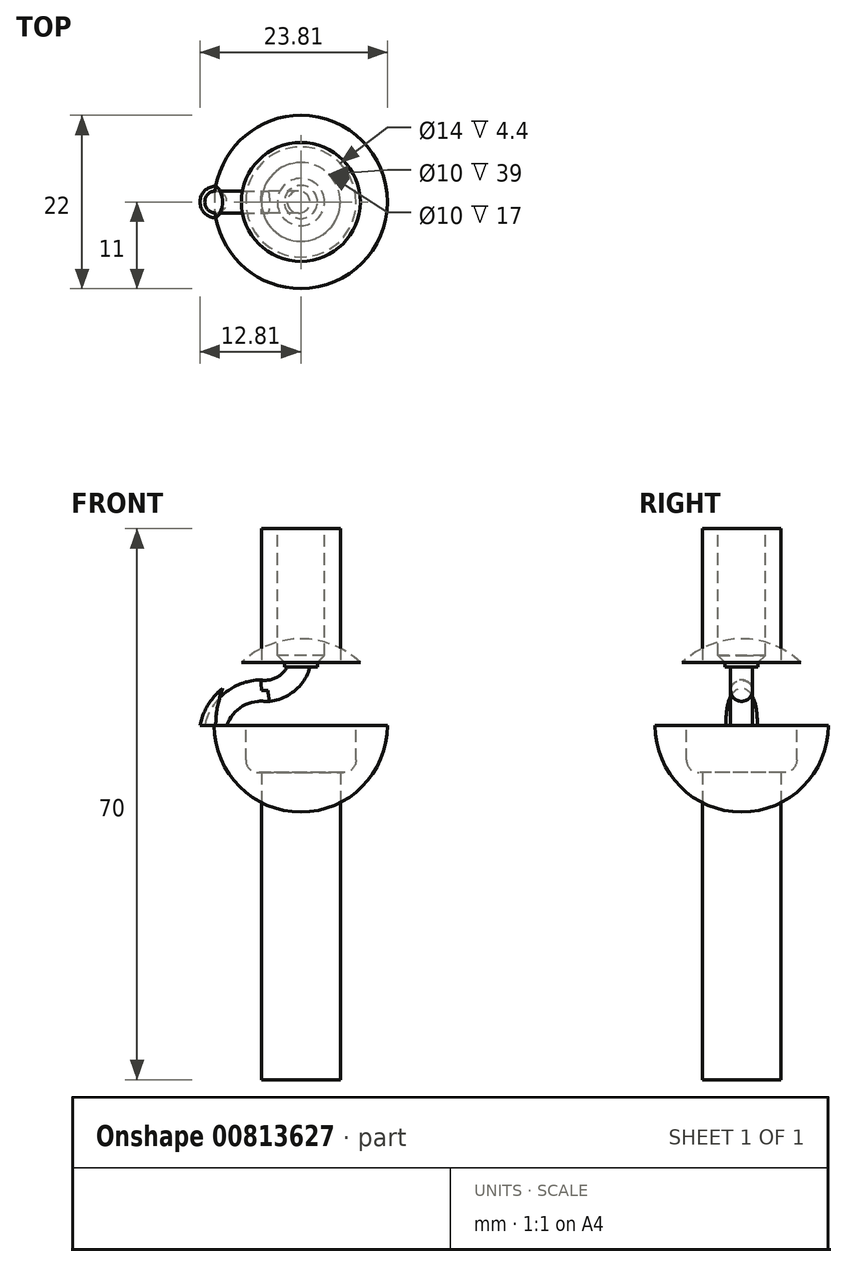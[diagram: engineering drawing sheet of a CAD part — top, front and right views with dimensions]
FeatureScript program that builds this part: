
annotation { "Feature Type Name" : "Feature", "Feature Type Description" : "" }
export const myFeature = defineFeature(function(context is Context, id is Id, definition is map)
    precondition{}
    {
        {
            var Q0;
            Q0=qCreatedBy(makeId("Top.planeOp"),FACE);
            var sketch = newSketch(context, id + "F0", { "sketchPlane" : qUnion([Q0])});
            skArc(sketch, "E0", {"start": v(6, 0) * mm, "mid": v(0, 6) * mm, "end": v(-6, 0) * mm});
            skLineSegment(sketch, "E1", {"start": v(-6, 0) * mm, "end": v(6, 0) * mm});
            skSolve(sketch);
        }
        {
            var Q0;
            Q0=makeQuery(id+"F0.imprint","IMPRINT",FACE,{"disambiguationData":[TD([[makeQuery(id+"F0.imprint","IMPRINT",EDGE,{"derivedFrom":sQuery(id+"F0.wireOp",EDGE,"E0")}),1.0]])]});
            var Q1;
            Q1=sQuery(id+"F0.wireOp",EDGE,"E1");
            revolve(context, id + "F1", {"surfaceOperationType" : NewSurfaceOperationType.NEW, "entities" : qUnion([Q0]), "axis" : qUnion([Q1]), "revolveType" : RevolveType.ONE_DIRECTION, "angle" : 180 * degree});
        }
        {
            var Q0;
            Q0=qCreatedBy(makeId("Front.planeOp"),FACE);
            var sketch = newSketch(context, id + "F2", { "sketchPlane" : qUnion([Q0])});
            skLineSegment(sketch, "E2.bottom", {"start": v(-10.2, 6.03) * mm, "end": v(11.74, 6.03) * mm});
            skLineSegment(sketch, "E2.top", {"start": v(-10.2, 4) * mm, "end": v(11.74, 4) * mm});
            skLineSegment(sketch, "E2.left", {"start": v(-10.2, 6.03) * mm, "end": v(-10.2, 4) * mm});
            skLineSegment(sketch, "E2.right", {"start": v(11.74, 6.03) * mm, "end": v(11.74, 4) * mm});
            skSolve(sketch);
        }
        {
            var Q0;
            Q0=qSketchRegion(id+"F2",true);
            extrude(context, id + "F3", {"entities" : qUnion([Q0]), "operationType" : NewBodyOperationType.REMOVE, "endBound" : BoundingType.SYMMETRIC, "depth" : 25 * mm, "offsetDistance" : 25 * mm});
        }
        {
            var Q0;
            Q0=qCreatedBy(makeId("Right.planeOp"),FACE);
            var sketch = newSketch(context, id + "F4", { "sketchPlane" : qUnion([Q0])});
            skLineSegment(sketch, "E3.bottom", {"start": v(5.5, 0.3) * mm, "end": v(5.3, 0.3) * mm});
            skLineSegment(sketch, "E3.top", {"start": v(5.5, 0.8) * mm, "end": v(5.3, 0.8) * mm});
            skLineSegment(sketch, "E3.left", {"start": v(5.5, 0.3) * mm, "end": v(5.5, 0.8) * mm});
            skLineSegment(sketch, "E3.right", {"start": v(5.3, 0.3) * mm, "end": v(5.3, 0.8) * mm});
            skLineSegment(sketch, "E4.0.1.0", {"start": v(5.3, 1.3) * mm, "end": v(5.3, 1.8) * mm});
            skLineSegment(sketch, "E4.0.1.1", {"start": v(5.5, 1.3) * mm, "end": v(5.5, 1.8) * mm});
            skLineSegment(sketch, "E4.0.1.2", {"start": v(5.5, 1.8) * mm, "end": v(5.3, 1.8) * mm});
            skLineSegment(sketch, "E4.0.1.3", {"start": v(5.5, 1.3) * mm, "end": v(5.3, 1.3) * mm});
            skLineSegment(sketch, "E4.0.2.0", {"start": v(5.3, 2.3) * mm, "end": v(5.3, 2.8) * mm});
            skLineSegment(sketch, "E4.0.2.1", {"start": v(5.5, 2.3) * mm, "end": v(5.5, 2.8) * mm});
            skLineSegment(sketch, "E4.0.2.2", {"start": v(5.5, 2.8) * mm, "end": v(5.3, 2.8) * mm});
            skLineSegment(sketch, "E4.0.2.3", {"start": v(5.5, 2.3) * mm, "end": v(5.3, 2.3) * mm});
            skLineSegment(sketch, "E4.0.3.0", {"start": v(5.3, 3.3) * mm, "end": v(5.3, 3.8) * mm});
            skLineSegment(sketch, "E4.0.3.1", {"start": v(5.5, 3.3) * mm, "end": v(5.5, 3.8) * mm});
            skLineSegment(sketch, "E4.0.3.2", {"start": v(5.5, 3.8) * mm, "end": v(5.3, 3.8) * mm});
            skLineSegment(sketch, "E4.0.3.3", {"start": v(5.5, 3.3) * mm, "end": v(5.3, 3.3) * mm});
            skLineSegment(sketch, "E4.1.0.0", {"start": v(4.22, 0.3) * mm, "end": v(4.22, 0.8) * mm});
            skLineSegment(sketch, "E4.1.0.1", {"start": v(4.42, 0.3) * mm, "end": v(4.42, 0.8) * mm});
            skLineSegment(sketch, "E4.1.0.2", {"start": v(4.42, 0.8) * mm, "end": v(4.22, 0.8) * mm});
            skLineSegment(sketch, "E4.1.0.3", {"start": v(4.42, 0.3) * mm, "end": v(4.22, 0.3) * mm});
            skLineSegment(sketch, "E4.1.1.0", {"start": v(4.22, 1.3) * mm, "end": v(4.22, 1.8) * mm});
            skLineSegment(sketch, "E4.1.1.1", {"start": v(4.42, 1.3) * mm, "end": v(4.42, 1.8) * mm});
            skLineSegment(sketch, "E4.1.1.2", {"start": v(4.42, 1.8) * mm, "end": v(4.22, 1.8) * mm});
            skLineSegment(sketch, "E4.1.1.3", {"start": v(4.42, 1.3) * mm, "end": v(4.22, 1.3) * mm});
            skLineSegment(sketch, "E4.1.2.0", {"start": v(4.22, 2.3) * mm, "end": v(4.22, 2.8) * mm});
            skLineSegment(sketch, "E4.1.2.1", {"start": v(4.42, 2.3) * mm, "end": v(4.42, 2.8) * mm});
            skLineSegment(sketch, "E4.1.2.2", {"start": v(4.42, 2.8) * mm, "end": v(4.22, 2.8) * mm});
            skLineSegment(sketch, "E4.1.2.3", {"start": v(4.42, 2.3) * mm, "end": v(4.22, 2.3) * mm});
            skLineSegment(sketch, "E4.1.3.0", {"start": v(4.22, 3.3) * mm, "end": v(4.22, 3.8) * mm});
            skLineSegment(sketch, "E4.1.3.1", {"start": v(4.42, 3.3) * mm, "end": v(4.42, 3.8) * mm});
            skLineSegment(sketch, "E4.1.3.2", {"start": v(4.42, 3.8) * mm, "end": v(4.22, 3.8) * mm});
            skLineSegment(sketch, "E4.1.3.3", {"start": v(4.42, 3.3) * mm, "end": v(4.22, 3.3) * mm});
            skLineSegment(sketch, "E4.2.0.0", {"start": v(3.14, 0.3) * mm, "end": v(3.14, 0.8) * mm});
            skLineSegment(sketch, "E4.2.0.1", {"start": v(3.34, 0.3) * mm, "end": v(3.34, 0.8) * mm});
            skLineSegment(sketch, "E4.2.0.2", {"start": v(3.34, 0.8) * mm, "end": v(3.14, 0.8) * mm});
            skLineSegment(sketch, "E4.2.0.3", {"start": v(3.34, 0.3) * mm, "end": v(3.14, 0.3) * mm});
            skLineSegment(sketch, "E4.2.1.0", {"start": v(3.14, 1.3) * mm, "end": v(3.14, 1.8) * mm});
            skLineSegment(sketch, "E4.2.1.1", {"start": v(3.34, 1.3) * mm, "end": v(3.34, 1.8) * mm});
            skLineSegment(sketch, "E4.2.1.2", {"start": v(3.34, 1.8) * mm, "end": v(3.14, 1.8) * mm});
            skLineSegment(sketch, "E4.2.1.3", {"start": v(3.34, 1.3) * mm, "end": v(3.14, 1.3) * mm});
            skLineSegment(sketch, "E4.2.2.0", {"start": v(3.14, 2.3) * mm, "end": v(3.14, 2.8) * mm});
            skLineSegment(sketch, "E4.2.2.1", {"start": v(3.34, 2.3) * mm, "end": v(3.34, 2.8) * mm});
            skLineSegment(sketch, "E4.2.2.2", {"start": v(3.34, 2.8) * mm, "end": v(3.14, 2.8) * mm});
            skLineSegment(sketch, "E4.2.2.3", {"start": v(3.34, 2.3) * mm, "end": v(3.14, 2.3) * mm});
            skLineSegment(sketch, "E4.2.3.0", {"start": v(3.14, 3.3) * mm, "end": v(3.14, 3.8) * mm});
            skLineSegment(sketch, "E4.2.3.1", {"start": v(3.34, 3.3) * mm, "end": v(3.34, 3.8) * mm});
            skLineSegment(sketch, "E4.2.3.2", {"start": v(3.34, 3.8) * mm, "end": v(3.14, 3.8) * mm});
            skLineSegment(sketch, "E4.2.3.3", {"start": v(3.34, 3.3) * mm, "end": v(3.14, 3.3) * mm});
            skLineSegment(sketch, "E4.3.0.0", {"start": v(2.06, 0.3) * mm, "end": v(2.06, 0.8) * mm});
            skLineSegment(sketch, "E4.3.0.1", {"start": v(2.26, 0.3) * mm, "end": v(2.26, 0.8) * mm});
            skLineSegment(sketch, "E4.3.0.2", {"start": v(2.26, 0.8) * mm, "end": v(2.06, 0.8) * mm});
            skLineSegment(sketch, "E4.3.0.3", {"start": v(2.26, 0.3) * mm, "end": v(2.06, 0.3) * mm});
            skLineSegment(sketch, "E4.3.1.0", {"start": v(2.06, 1.3) * mm, "end": v(2.06, 1.8) * mm});
            skLineSegment(sketch, "E4.3.1.1", {"start": v(2.26, 1.3) * mm, "end": v(2.26, 1.8) * mm});
            skLineSegment(sketch, "E4.3.1.2", {"start": v(2.26, 1.8) * mm, "end": v(2.06, 1.8) * mm});
            skLineSegment(sketch, "E4.3.1.3", {"start": v(2.26, 1.3) * mm, "end": v(2.06, 1.3) * mm});
            skLineSegment(sketch, "E4.3.2.0", {"start": v(2.06, 2.3) * mm, "end": v(2.06, 2.8) * mm});
            skLineSegment(sketch, "E4.3.2.1", {"start": v(2.26, 2.3) * mm, "end": v(2.26, 2.8) * mm});
            skLineSegment(sketch, "E4.3.2.2", {"start": v(2.26, 2.8) * mm, "end": v(2.06, 2.8) * mm});
            skLineSegment(sketch, "E4.3.2.3", {"start": v(2.26, 2.3) * mm, "end": v(2.06, 2.3) * mm});
            skLineSegment(sketch, "E4.3.3.0", {"start": v(2.06, 3.3) * mm, "end": v(2.06, 3.8) * mm});
            skLineSegment(sketch, "E4.3.3.1", {"start": v(2.26, 3.3) * mm, "end": v(2.26, 3.8) * mm});
            skLineSegment(sketch, "E4.3.3.2", {"start": v(2.26, 3.8) * mm, "end": v(2.06, 3.8) * mm});
            skLineSegment(sketch, "E4.3.3.3", {"start": v(2.26, 3.3) * mm, "end": v(2.06, 3.3) * mm});
            skLineSegment(sketch, "E4.4.0.0", {"start": v(0.98, 0.3) * mm, "end": v(0.98, 0.8) * mm});
            skLineSegment(sketch, "E4.4.0.1", {"start": v(1.18, 0.3) * mm, "end": v(1.18, 0.8) * mm});
            skLineSegment(sketch, "E4.4.0.2", {"start": v(1.18, 0.8) * mm, "end": v(0.98, 0.8) * mm});
            skLineSegment(sketch, "E4.4.0.3", {"start": v(1.18, 0.3) * mm, "end": v(0.98, 0.3) * mm});
            skLineSegment(sketch, "E4.4.1.0", {"start": v(0.98, 1.3) * mm, "end": v(0.98, 1.8) * mm});
            skLineSegment(sketch, "E4.4.1.1", {"start": v(1.18, 1.3) * mm, "end": v(1.18, 1.8) * mm});
            skLineSegment(sketch, "E4.4.1.2", {"start": v(1.18, 1.8) * mm, "end": v(0.98, 1.8) * mm});
            skLineSegment(sketch, "E4.4.1.3", {"start": v(1.18, 1.3) * mm, "end": v(0.98, 1.3) * mm});
            skLineSegment(sketch, "E4.4.2.0", {"start": v(0.98, 2.3) * mm, "end": v(0.98, 2.8) * mm});
            skLineSegment(sketch, "E4.4.2.1", {"start": v(1.18, 2.3) * mm, "end": v(1.18, 2.8) * mm});
            skLineSegment(sketch, "E4.4.2.2", {"start": v(1.18, 2.8) * mm, "end": v(0.98, 2.8) * mm});
            skLineSegment(sketch, "E4.4.2.3", {"start": v(1.18, 2.3) * mm, "end": v(0.98, 2.3) * mm});
            skLineSegment(sketch, "E4.4.3.0", {"start": v(0.98, 3.3) * mm, "end": v(0.98, 3.8) * mm});
            skLineSegment(sketch, "E4.4.3.1", {"start": v(1.18, 3.3) * mm, "end": v(1.18, 3.8) * mm});
            skLineSegment(sketch, "E4.4.3.2", {"start": v(1.18, 3.8) * mm, "end": v(0.98, 3.8) * mm});
            skLineSegment(sketch, "E4.4.3.3", {"start": v(1.18, 3.3) * mm, "end": v(0.98, 3.3) * mm});
            skLineSegment(sketch, "E4.5.0.0", {"start": v(-0.1, 0.3) * mm, "end": v(-0.1, 0.8) * mm});
            skLineSegment(sketch, "E4.5.0.1", {"start": v(0.1, 0.3) * mm, "end": v(0.1, 0.8) * mm});
            skLineSegment(sketch, "E4.5.0.2", {"start": v(0.1, 0.8) * mm, "end": v(-0.1, 0.8) * mm});
            skLineSegment(sketch, "E4.5.0.3", {"start": v(0.1, 0.3) * mm, "end": v(-0.1, 0.3) * mm});
            skLineSegment(sketch, "E4.5.1.0", {"start": v(-0.1, 1.3) * mm, "end": v(-0.1, 1.8) * mm});
            skLineSegment(sketch, "E4.5.1.1", {"start": v(0.1, 1.3) * mm, "end": v(0.1, 1.8) * mm});
            skLineSegment(sketch, "E4.5.1.2", {"start": v(0.1, 1.8) * mm, "end": v(-0.1, 1.8) * mm});
            skLineSegment(sketch, "E4.5.1.3", {"start": v(0.1, 1.3) * mm, "end": v(-0.1, 1.3) * mm});
            skLineSegment(sketch, "E4.5.2.0", {"start": v(-0.1, 2.3) * mm, "end": v(-0.1, 2.8) * mm});
            skLineSegment(sketch, "E4.5.2.1", {"start": v(0.1, 2.3) * mm, "end": v(0.1, 2.8) * mm});
            skLineSegment(sketch, "E4.5.2.2", {"start": v(0.1, 2.8) * mm, "end": v(-0.1, 2.8) * mm});
            skLineSegment(sketch, "E4.5.2.3", {"start": v(0.1, 2.3) * mm, "end": v(-0.1, 2.3) * mm});
            skLineSegment(sketch, "E4.5.3.0", {"start": v(-0.1, 3.3) * mm, "end": v(-0.1, 3.8) * mm});
            skLineSegment(sketch, "E4.5.3.1", {"start": v(0.1, 3.3) * mm, "end": v(0.1, 3.8) * mm});
            skLineSegment(sketch, "E4.5.3.2", {"start": v(0.1, 3.8) * mm, "end": v(-0.1, 3.8) * mm});
            skLineSegment(sketch, "E4.5.3.3", {"start": v(0.1, 3.3) * mm, "end": v(-0.1, 3.3) * mm});
            skLineSegment(sketch, "E4.6.0.0", {"start": v(-1.18, 0.3) * mm, "end": v(-1.18, 0.8) * mm});
            skLineSegment(sketch, "E4.6.0.1", {"start": v(-0.98, 0.3) * mm, "end": v(-0.98, 0.8) * mm});
            skLineSegment(sketch, "E4.6.0.2", {"start": v(-0.98, 0.8) * mm, "end": v(-1.18, 0.8) * mm});
            skLineSegment(sketch, "E4.6.0.3", {"start": v(-0.98, 0.3) * mm, "end": v(-1.18, 0.3) * mm});
            skLineSegment(sketch, "E4.6.1.0", {"start": v(-1.18, 1.3) * mm, "end": v(-1.18, 1.8) * mm});
            skLineSegment(sketch, "E4.6.1.1", {"start": v(-0.98, 1.3) * mm, "end": v(-0.98, 1.8) * mm});
            skLineSegment(sketch, "E4.6.1.2", {"start": v(-0.98, 1.8) * mm, "end": v(-1.18, 1.8) * mm});
            skLineSegment(sketch, "E4.6.1.3", {"start": v(-0.98, 1.3) * mm, "end": v(-1.18, 1.3) * mm});
            skLineSegment(sketch, "E4.6.2.0", {"start": v(-1.18, 2.3) * mm, "end": v(-1.18, 2.8) * mm});
            skLineSegment(sketch, "E4.6.2.1", {"start": v(-0.98, 2.3) * mm, "end": v(-0.98, 2.8) * mm});
            skLineSegment(sketch, "E4.6.2.2", {"start": v(-0.98, 2.8) * mm, "end": v(-1.18, 2.8) * mm});
            skLineSegment(sketch, "E4.6.2.3", {"start": v(-0.98, 2.3) * mm, "end": v(-1.18, 2.3) * mm});
            skLineSegment(sketch, "E4.6.3.0", {"start": v(-1.18, 3.3) * mm, "end": v(-1.18, 3.8) * mm});
            skLineSegment(sketch, "E4.6.3.1", {"start": v(-0.98, 3.3) * mm, "end": v(-0.98, 3.8) * mm});
            skLineSegment(sketch, "E4.6.3.2", {"start": v(-0.98, 3.8) * mm, "end": v(-1.18, 3.8) * mm});
            skLineSegment(sketch, "E4.6.3.3", {"start": v(-0.98, 3.3) * mm, "end": v(-1.18, 3.3) * mm});
            skLineSegment(sketch, "E4.7.0.0", {"start": v(-2.26, 0.3) * mm, "end": v(-2.26, 0.8) * mm});
            skLineSegment(sketch, "E4.7.0.1", {"start": v(-2.06, 0.3) * mm, "end": v(-2.06, 0.8) * mm});
            skLineSegment(sketch, "E4.7.0.2", {"start": v(-2.06, 0.8) * mm, "end": v(-2.26, 0.8) * mm});
            skLineSegment(sketch, "E4.7.0.3", {"start": v(-2.06, 0.3) * mm, "end": v(-2.26, 0.3) * mm});
            skLineSegment(sketch, "E4.7.1.0", {"start": v(-2.26, 1.3) * mm, "end": v(-2.26, 1.8) * mm});
            skLineSegment(sketch, "E4.7.1.1", {"start": v(-2.06, 1.3) * mm, "end": v(-2.06, 1.8) * mm});
            skLineSegment(sketch, "E4.7.1.2", {"start": v(-2.06, 1.8) * mm, "end": v(-2.26, 1.8) * mm});
            skLineSegment(sketch, "E4.7.1.3", {"start": v(-2.06, 1.3) * mm, "end": v(-2.26, 1.3) * mm});
            skLineSegment(sketch, "E4.7.2.0", {"start": v(-2.26, 2.3) * mm, "end": v(-2.26, 2.8) * mm});
            skLineSegment(sketch, "E4.7.2.1", {"start": v(-2.06, 2.3) * mm, "end": v(-2.06, 2.8) * mm});
            skLineSegment(sketch, "E4.7.2.2", {"start": v(-2.06, 2.8) * mm, "end": v(-2.26, 2.8) * mm});
            skLineSegment(sketch, "E4.7.2.3", {"start": v(-2.06, 2.3) * mm, "end": v(-2.26, 2.3) * mm});
            skLineSegment(sketch, "E4.7.3.0", {"start": v(-2.26, 3.3) * mm, "end": v(-2.26, 3.8) * mm});
            skLineSegment(sketch, "E4.7.3.1", {"start": v(-2.06, 3.3) * mm, "end": v(-2.06, 3.8) * mm});
            skLineSegment(sketch, "E4.7.3.2", {"start": v(-2.06, 3.8) * mm, "end": v(-2.26, 3.8) * mm});
            skLineSegment(sketch, "E4.7.3.3", {"start": v(-2.06, 3.3) * mm, "end": v(-2.26, 3.3) * mm});
            skLineSegment(sketch, "E4.8.0.0", {"start": v(-3.34, 0.3) * mm, "end": v(-3.34, 0.8) * mm});
            skLineSegment(sketch, "E4.8.0.1", {"start": v(-3.14, 0.3) * mm, "end": v(-3.14, 0.8) * mm});
            skLineSegment(sketch, "E4.8.0.2", {"start": v(-3.14, 0.8) * mm, "end": v(-3.34, 0.8) * mm});
            skLineSegment(sketch, "E4.8.0.3", {"start": v(-3.14, 0.3) * mm, "end": v(-3.34, 0.3) * mm});
            skLineSegment(sketch, "E4.8.1.0", {"start": v(-3.34, 1.3) * mm, "end": v(-3.34, 1.8) * mm});
            skLineSegment(sketch, "E4.8.1.1", {"start": v(-3.14, 1.3) * mm, "end": v(-3.14, 1.8) * mm});
            skLineSegment(sketch, "E4.8.1.2", {"start": v(-3.14, 1.8) * mm, "end": v(-3.34, 1.8) * mm});
            skLineSegment(sketch, "E4.8.1.3", {"start": v(-3.14, 1.3) * mm, "end": v(-3.34, 1.3) * mm});
            skLineSegment(sketch, "E4.8.2.0", {"start": v(-3.34, 2.3) * mm, "end": v(-3.34, 2.8) * mm});
            skLineSegment(sketch, "E4.8.2.1", {"start": v(-3.14, 2.3) * mm, "end": v(-3.14, 2.8) * mm});
            skLineSegment(sketch, "E4.8.2.2", {"start": v(-3.14, 2.8) * mm, "end": v(-3.34, 2.8) * mm});
            skLineSegment(sketch, "E4.8.2.3", {"start": v(-3.14, 2.3) * mm, "end": v(-3.34, 2.3) * mm});
            skLineSegment(sketch, "E4.8.3.0", {"start": v(-3.34, 3.3) * mm, "end": v(-3.34, 3.8) * mm});
            skLineSegment(sketch, "E4.8.3.1", {"start": v(-3.14, 3.3) * mm, "end": v(-3.14, 3.8) * mm});
            skLineSegment(sketch, "E4.8.3.2", {"start": v(-3.14, 3.8) * mm, "end": v(-3.34, 3.8) * mm});
            skLineSegment(sketch, "E4.8.3.3", {"start": v(-3.14, 3.3) * mm, "end": v(-3.34, 3.3) * mm});
            skLineSegment(sketch, "E4.9.0.0", {"start": v(-4.42, 0.3) * mm, "end": v(-4.42, 0.8) * mm});
            skLineSegment(sketch, "E4.9.0.1", {"start": v(-4.22, 0.3) * mm, "end": v(-4.22, 0.8) * mm});
            skLineSegment(sketch, "E4.9.0.2", {"start": v(-4.22, 0.8) * mm, "end": v(-4.42, 0.8) * mm});
            skLineSegment(sketch, "E4.9.0.3", {"start": v(-4.22, 0.3) * mm, "end": v(-4.42, 0.3) * mm});
            skLineSegment(sketch, "E4.9.1.0", {"start": v(-4.42, 1.3) * mm, "end": v(-4.42, 1.8) * mm});
            skLineSegment(sketch, "E4.9.1.1", {"start": v(-4.22, 1.3) * mm, "end": v(-4.22, 1.8) * mm});
            skLineSegment(sketch, "E4.9.1.2", {"start": v(-4.22, 1.8) * mm, "end": v(-4.42, 1.8) * mm});
            skLineSegment(sketch, "E4.9.1.3", {"start": v(-4.22, 1.3) * mm, "end": v(-4.42, 1.3) * mm});
            skLineSegment(sketch, "E4.9.2.0", {"start": v(-4.42, 2.3) * mm, "end": v(-4.42, 2.8) * mm});
            skLineSegment(sketch, "E4.9.2.1", {"start": v(-4.22, 2.3) * mm, "end": v(-4.22, 2.8) * mm});
            skLineSegment(sketch, "E4.9.2.2", {"start": v(-4.22, 2.8) * mm, "end": v(-4.42, 2.8) * mm});
            skLineSegment(sketch, "E4.9.2.3", {"start": v(-4.22, 2.3) * mm, "end": v(-4.42, 2.3) * mm});
            skLineSegment(sketch, "E4.9.3.0", {"start": v(-4.42, 3.3) * mm, "end": v(-4.42, 3.8) * mm});
            skLineSegment(sketch, "E4.9.3.1", {"start": v(-4.22, 3.3) * mm, "end": v(-4.22, 3.8) * mm});
            skLineSegment(sketch, "E4.9.3.2", {"start": v(-4.22, 3.8) * mm, "end": v(-4.42, 3.8) * mm});
            skLineSegment(sketch, "E4.9.3.3", {"start": v(-4.22, 3.3) * mm, "end": v(-4.42, 3.3) * mm});
            skLineSegment(sketch, "E4.10.0.0", {"start": v(-5.5, 0.3) * mm, "end": v(-5.5, 0.8) * mm});
            skLineSegment(sketch, "E4.10.0.1", {"start": v(-5.3, 0.3) * mm, "end": v(-5.3, 0.8) * mm});
            skLineSegment(sketch, "E4.10.0.2", {"start": v(-5.3, 0.8) * mm, "end": v(-5.5, 0.8) * mm});
            skLineSegment(sketch, "E4.10.0.3", {"start": v(-5.3, 0.3) * mm, "end": v(-5.5, 0.3) * mm});
            skLineSegment(sketch, "E4.10.1.0", {"start": v(-5.5, 1.3) * mm, "end": v(-5.5, 1.8) * mm});
            skLineSegment(sketch, "E4.10.1.1", {"start": v(-5.3, 1.3) * mm, "end": v(-5.3, 1.8) * mm});
            skLineSegment(sketch, "E4.10.1.2", {"start": v(-5.3, 1.8) * mm, "end": v(-5.5, 1.8) * mm});
            skLineSegment(sketch, "E4.10.1.3", {"start": v(-5.3, 1.3) * mm, "end": v(-5.5, 1.3) * mm});
            skLineSegment(sketch, "E4.10.2.0", {"start": v(-5.5, 2.3) * mm, "end": v(-5.5, 2.8) * mm});
            skLineSegment(sketch, "E4.10.2.1", {"start": v(-5.3, 2.3) * mm, "end": v(-5.3, 2.8) * mm});
            skLineSegment(sketch, "E4.10.2.2", {"start": v(-5.3, 2.8) * mm, "end": v(-5.5, 2.8) * mm});
            skLineSegment(sketch, "E4.10.2.3", {"start": v(-5.3, 2.3) * mm, "end": v(-5.5, 2.3) * mm});
            skLineSegment(sketch, "E4.10.3.0", {"start": v(-5.5, 3.3) * mm, "end": v(-5.5, 3.8) * mm});
            skLineSegment(sketch, "E4.10.3.1", {"start": v(-5.3, 3.3) * mm, "end": v(-5.3, 3.8) * mm});
            skLineSegment(sketch, "E4.10.3.2", {"start": v(-5.3, 3.8) * mm, "end": v(-5.5, 3.8) * mm});
            skLineSegment(sketch, "E4.10.3.3", {"start": v(-5.3, 3.3) * mm, "end": v(-5.5, 3.3) * mm});
            skLineSegment(sketch, "E4.direction1", {"start": v(5.3, 0.3) * mm, "end": v(4.22, 0.3) * mm, "construction": true});
            skLineSegment(sketch, "E4.direction2", {"start": v(5.3, 0.3) * mm, "end": v(5.3, 1.3) * mm, "construction": true});
            skSolve(sketch);
        }
        {
            var Q0;
            Q0=qSketchRegion(id+"F4",true);
            extrude(context, id + "F5", {"entities" : qUnion([Q0]), "operationType" : NewBodyOperationType.ADD, "endBound" : BoundingType.SYMMETRIC, "depth" : 25 * mm, "offsetDistance" : 25 * mm});
        }
        {
            var Q0;
            Q0=qCreatedBy(makeId("Top.planeOp"),FACE);
            var sketch = newSketch(context, id + "F6", { "sketchPlane" : qUnion([Q0])});
            skArc(sketch, "E5", {"start": v(0, 5.5) * mm, "mid": v(-5.5, 0) * mm, "end": v(0, -5.5) * mm});
            skLineSegment(sketch, "E6", {"start": v(0, -5.5) * mm, "end": v(0, -15.7) * mm});
            skLineSegment(sketch, "E7", {"start": v(0, 5.5) * mm, "end": v(0, 15.7) * mm});
            skArc(sketch, "E8", {"start": v(0, 15.7) * mm, "mid": v(-15.7, 0) * mm, "end": v(0, -15.7) * mm});
            skSolve(sketch);
        }
        {
            var Q0;
            Q0=qCreatedBy(makeId("Top.planeOp"),FACE);
            var sketch = newSketch(context, id + "F7", { "sketchPlane" : qUnion([Q0])});
            skLineSegment(sketch, "E9", {"start": v(0, 43.35) * mm, "end": v(0, -56.08) * mm, "construction": true});
            skSolve(sketch);
        }
        {
            var Q0;
            Q0=qSketchRegion(id+"F6",true);
            var Q1;
            Q1=sQuery(id+"F7.wireOp",EDGE,"E9");
            revolve(context, id + "F8", {"operationType" : NewBodyOperationType.REMOVE, "surfaceOperationType" : NewSurfaceOperationType.NEW, "entities" : qUnion([Q0]), "axis" : qUnion([Q1]), "revolveType" : RevolveType.ONE_DIRECTION, "oppositeDirection" : true, "angle" : 180 * degree});
        }
        {
            var Q0;
            Q0=qCreatedBy(makeId("Top.planeOp"),FACE);
            var sketch = newSketch(context, id + "F9", { "sketchPlane" : qUnion([Q0])});
            skCircle(sketch, "E10", {"center": v(0, 0) * mm, "radius": 2.5 * mm});
            skSolve(sketch);
        }
        {
            var Q0;
            Q0=qSketchRegion(id+"F9",true);
            extrude(context, id + "F10", {"entities" : qUnion([Q0]), "operationType" : NewBodyOperationType.ADD, "endBound" : BoundingType.SYMMETRIC, "depth" : 25 * mm, "offsetDistance" : 25 * mm});
        }
        {
            var Q0;
            Q0=makeQuery(id+"F10.opExtrude","CAP_FACE",FACE,{"disambiguationData":[OSD([sQuery(id+"F9.wireOp",EDGE,"E10")])],"isStart":false});
            var sketch = newSketch(context, id + "F11", { "sketchPlane" : qUnion([Q0])});
            skCircle(sketch, "E11", {"center": v(0, 0) * mm, "radius": 1.5 * mm});
            skSolve(sketch);
        }
        {
            var Q0;
            Q0=makeQuery(id+"F11.imprint","IMPRINT",FACE,{"disambiguationData":[TD([[makeQuery(id+"F11.imprint","IMPRINT",EDGE,{"derivedFrom":sQuery(id+"F11.wireOp",EDGE,"E11")}),1.0]])]});
            extrude(context, id + "F12", {"entities" : qUnion([Q0]), "operationType" : NewBodyOperationType.REMOVE, "oppositeDirection" : true, "depth" : 8 * mm, "offsetDistance" : 25 * mm});
        }
        {
            var Q0;
            Q0=makeQuery(id+"F1.opRevolve","CAP_FACE",FACE,{"disambiguationData":[OSD([sQuery(id+"F0.wireOp",EDGE,"E0"),sQuery(id+"F0.wireOp",EDGE,"E1")])],"isStart":true});
            var sketch = newSketch(context, id + "F13", { "sketchPlane" : qUnion([Q0])});
            skCircle(sketch, "E12", {"center": v(0, 0) * mm, "radius": 3.5 * mm});
            skSolve(sketch);
        }
        {
            var Q0;
            Q0=qSketchRegion(id+"F13",true);
            extrude(context, id + "F14", {"entities" : qUnion([Q0]), "operationType" : NewBodyOperationType.ADD, "depth" : 3 * mm, "offsetDistance" : 25 * mm});
        }
        {
            var Q0;
            Q0=makeQuery(id+"F14.opExtrude","CAP_EDGE",EDGE,{"disambiguationData":[OSD([sQuery(id+"F13.wireOp",EDGE,"E12")])],"isStart":false});
            fillet(context, id + "F15", {"entities" : qUnion([Q0]), "radius" : 0.8 * mm, "tangentPropagation" : true, "allowEdgeOverflow" : false});
        }
        {
            var Q0;
            Q0=makeQuery(id+"F10.opExtrude","CAP_FACE",FACE,{"disambiguationData":[OSD([sQuery(id+"F9.wireOp",EDGE,"E10")])],"isStart":true});
            var sketch = newSketch(context, id + "F16", { "sketchPlane" : qUnion([Q0])});
            skCircle(sketch, "E13", {"center": v(0, 0) * mm, "radius": 2.5 * mm});
            skSolve(sketch);
        }
        {
            var Q0;
            Q0=qSketchRegion(id+"F16",true);
            extrude(context, id + "F17", {"entities" : qUnion([Q0]), "operationType" : NewBodyOperationType.ADD, "depth" : 10 * mm, "offsetDistance" : 25 * mm});
        }
        {
            var Q0;
            Q0=qCreatedBy(makeId("Front.planeOp"),FACE);
            var sketch = newSketch(context, id + "F18", { "sketchPlane" : qUnion([Q0])});
            skArc(sketch, "E14", {"start": v(-2.5, 2.23) * mm, "mid": v(-4.33, 1.6) * mm, "end": v(-5.4, 0) * mm});
            skArc(sketch, "E15", {"start": v(-2.5, 2.23) * mm, "mid": v(-0.75, 2.83) * mm, "end": v(0, 4.52) * mm});
            skSolve(sketch);
        }
        {
            var Q0;
            Q0=qCreatedBy(makeId("Top.planeOp"),FACE);
            var sketch = newSketch(context, id + "F19", { "sketchPlane" : qUnion([Q0])});
            skCircle(sketch, "E16", {"center": v(-5.4, 0) * mm, "radius": 1 * mm});
            skSolve(sketch);
        }
        {
            var Q0;
            Q0=makeQuery(id+"F19.imprint","IMPRINT",FACE,{"disambiguationData":[TD([[makeQuery(id+"F19.imprint","IMPRINT",EDGE,{"derivedFrom":sQuery(id+"F19.wireOp",EDGE,"E16")}),1.0]])]});
            var Q1;
            Q1=sQuery(id+"F18.wireOp",EDGE,"E14");
            var Q2;
            Q2=sQuery(id+"F18.wireOp",EDGE,"E15");
            sweep(context, id + "F20", {"operationType" : NewBodyOperationType.ADD, "profiles" : qUnion([Q0]), "path" : qUnion([Q1, Q2])});
        }
        {
            var Q0;
            Q0=makeQuery(id+"F20.boolean.opBoolean","MERGE",FACE,{"derivedFrom":[makeQuery(id+"F1.opRevolve","CAP_FACE",FACE,{"disambiguationData":[OSD([sQuery(id+"F0.wireOp",EDGE,"E0"),sQuery(id+"F0.wireOp",EDGE,"E1")])],"isStart":true}),makeQuery(id+"F20.opSweep","CAP_FACE",FACE,{"disambiguationData":[OSD([sQuery(id+"F18.wireOp",VERTEX,"E14.end"),sQuery(id+"F19.wireOp",EDGE,"E16")])],"isStart":true})]});
            var sketch = newSketch(context, id + "F21", { "sketchPlane" : qUnion([Q0])});
            skCircle(sketch, "E17", {"center": v(-5.4, 0) * mm, "radius": 0.7 * mm});
            skSolve(sketch);
        }
        {
            var Q0;
            Q0=makeQuery(id+"F12.boolean.opBoolean","COPY",FACE,{"derivedFrom":makeQuery(id+"F12.opExtrude","CAP_FACE",FACE,{"disambiguationData":[OSD([sQuery(id+"F11.wireOp",EDGE,"E11")])],"isStart":false})});
            var sketch = newSketch(context, id + "F22", { "sketchPlane" : qUnion([Q0])});
            skPoint(sketch, "E18", {"position": v(0, 0) * mm});
            skSolve(sketch);
        }
        {
            var Q0;
            Q0=qCreatedBy(makeId("Front.planeOp"),FACE);
            var sketch = newSketch(context, id + "F23", { "sketchPlane" : qUnion([Q0])});
            skArc(sketch, "E19", {"start": v(-2.51, 2.2) * mm, "mid": v(-4.33, 1.6) * mm, "end": v(-5.4, 0) * mm});
            skArc(sketch, "E20", {"start": v(-2.51, 2.2) * mm, "mid": v(-0.75, 2.8) * mm, "end": v(0, 4.5) * mm});
            skSolve(sketch);
        }
        {
            var Q0;
            Q0=makeQuery(id+"F21.imprint","IMPRINT",FACE,{"disambiguationData":[TD([[makeQuery(id+"F21.imprint","IMPRINT",EDGE,{"derivedFrom":sQuery(id+"F21.wireOp",EDGE,"E17")}),1.0]])]});
            var Q1;
            Q1=sQuery(id+"F23.wireOp",EDGE,"E19");
            var Q2;
            Q2=sQuery(id+"F23.wireOp",EDGE,"E20");
            sweep(context, id + "F24", {"operationType" : NewBodyOperationType.REMOVE, "profiles" : qUnion([Q0]), "path" : qUnion([Q1, Q2])});
        }
        {
            var Q0;
            {var subQ0=sQuery(id+"F11.wireOp",EDGE,"E11");Q0=makeQuery(id+"F22.imprint","IMPRINT",FACE,{"disambiguationData":[TD([[makeQuery(id+"F22.imprint","IMPRINT",EDGE,{"derivedFrom":makeQuery(id+"F12.boolean.opBoolean","COPY",EDGE,{"derivedFrom":makeQuery(id+"F12.opExtrude","CAP_EDGE",EDGE,{"disambiguationData":[OSD([subQ0])],"isStart":false})})}),1.0]])]});}
            var sketch = newSketch(context, id + "F25", { "sketchPlane" : qUnion([Q0])});
            skCircle(sketch, "E21", {"center": v(0, 0) * mm, "radius": 1.05 * mm});
            skSolve(sketch);
        }
        {
            var Q0;
            Q0=qSketchRegion(id+"F25",true);
            extrude(context, id + "F26", {"entities" : qUnion([Q0]), "operationType" : NewBodyOperationType.REMOVE, "oppositeDirection" : true, "depth" : 0.8 * mm, "offsetDistance" : 25 * mm, "hasSecondDirection" : true, "secondDirectionOppositeDirection" : false, "secondDirectionDepth" : 25 * mm});
        }
        {
            var Q0;
            Q0=makeQuery(id+"F26.boolean.opBoolean","INTERSECT",EDGE,{"derivedFrom":[makeQuery(id+"F12.boolean.opBoolean","COPY",FACE,{"derivedFrom":makeQuery(id+"F12.opExtrude","CAP_FACE",FACE,{"disambiguationData":[OSD([sQuery(id+"F11.wireOp",EDGE,"E11")])],"isStart":false})}),makeQuery(id+"F26.opExtrude","SWEPT_FACE",FACE,{"disambiguationData":[OSD([sQuery(id+"F25.wireOp",EDGE,"E21")])]})]});
            chamfer(context, id + "F27", {"entities" : qUnion([Q0]), "width" : 0.5 * mm, "tangentPropagation" : true});
        }
        {
            var Q0;
            Q0=makeQuery(id+"F1.opRevolve","SWEPT_BODY",BODY,{"disambiguationData":[OSD([sQuery(id+"F0.wireOp",EDGE,"E0"),sQuery(id+"F0.wireOp",EDGE,"E1")])]});
            var Q1;
            Q1=qCreatedBy(makeId("Origin.pointOp"),VERTEX);
            var Q2;
            Q2=qCreatedBy(makeId("Origin.pointOp"),VERTEX);
            transform(context, id + "F28", {"entities" : qUnion([Q0]), "transformType" : TransformType.SCALE_UNIFORMLY, "scale" : 2, "scalePoint" : qUnion([Q2]), "makeCopy" : false});
        }
    });
